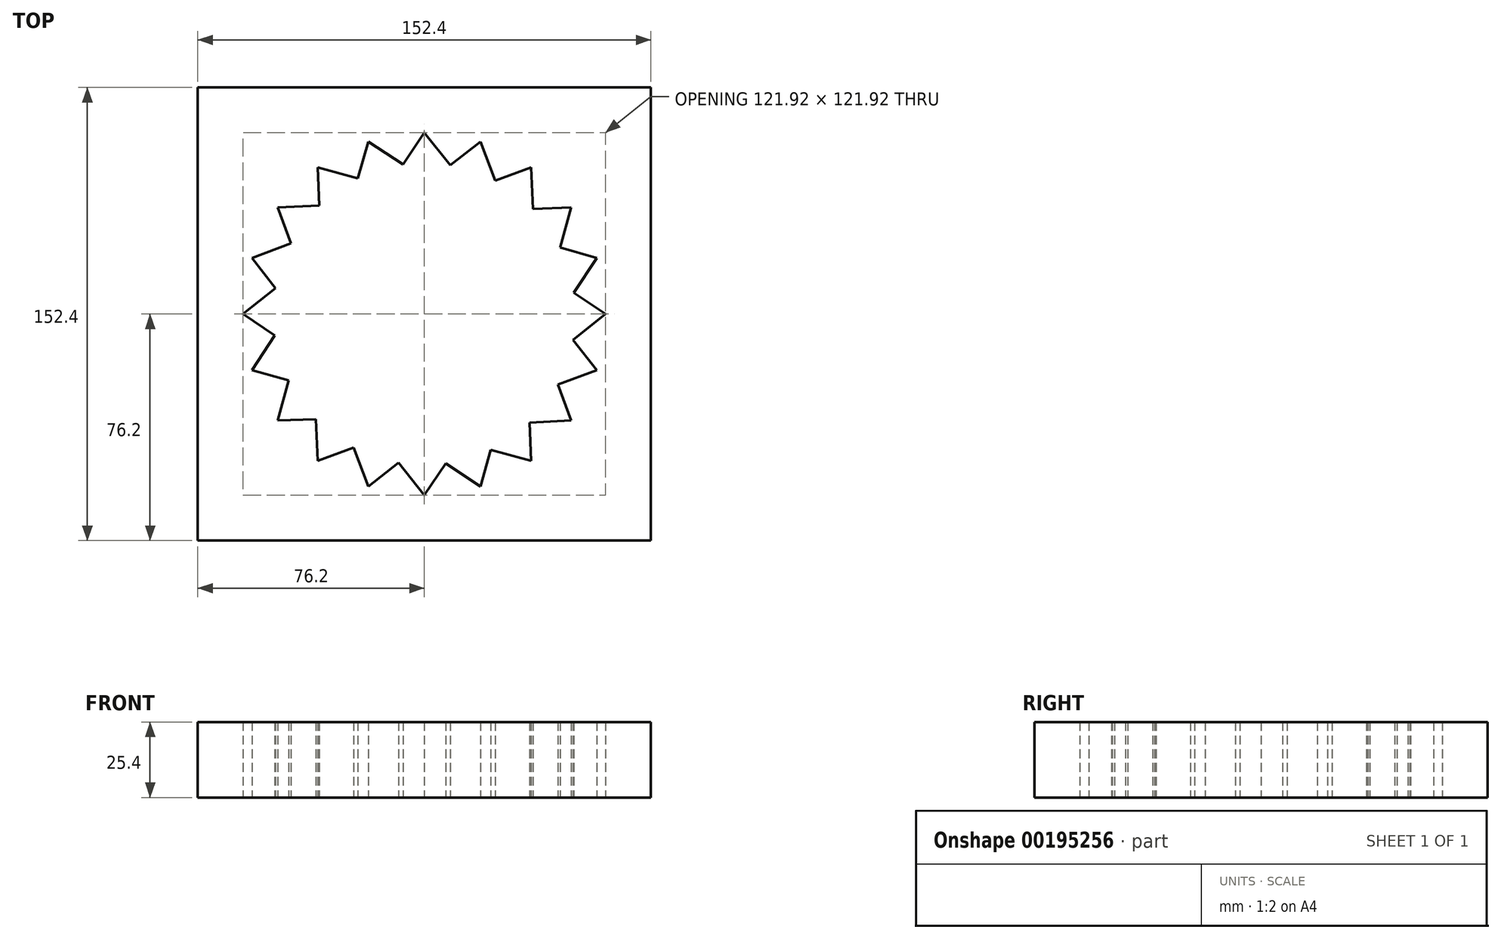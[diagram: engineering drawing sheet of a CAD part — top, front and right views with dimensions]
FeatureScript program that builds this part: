
annotation { "Feature Type Name" : "Feature", "Feature Type Description" : "" }
export const myFeature = defineFeature(function(context is Context, id is Id, definition is map)
    precondition{}
    {
        {
            var Q0;
            Q0=qCreatedBy(makeId("Top.planeOp"),FACE);
            var sketch = newSketch(context, id + "F0", { "sketchPlane" : qUnion([Q0])});
            skLineSegment(sketch, "E0.bottom", {"start": v(-76.2, -76.2) * mm, "end": v(76.2, -76.2) * mm});
            skLineSegment(sketch, "E0.top", {"start": v(-76.2, 76.2) * mm, "end": v(76.2, 76.2) * mm});
            skLineSegment(sketch, "E0.left", {"start": v(-76.2, -76.2) * mm, "end": v(-76.2, 76.2) * mm});
            skLineSegment(sketch, "E0.right", {"start": v(76.2, -76.2) * mm, "end": v(76.2, 76.2) * mm});
            skPoint(sketch, "E1", {"position": v(0, 50.8) * mm});
            skPoint(sketch, "E2", {"position": v(0, 60.96) * mm});
            skLineSegment(sketch, "E3", {"start": v(0, 60.96) * mm, "end": v(-7.15, 50.3) * mm});
            skLineSegment(sketch, "E4", {"start": v(8.74, 50.04) * mm, "end": v(0, 60.96) * mm});
            skLineSegment(sketch, "E5.1.0", {"start": v(-7.15, 50.3) * mm, "end": v(-18.84, 57.98) * mm});
            skLineSegment(sketch, "E5.1.1", {"start": v(-18.84, 57.98) * mm, "end": v(-22.35, 45.62) * mm});
            skLineSegment(sketch, "E5.2.0", {"start": v(-22.35, 45.62) * mm, "end": v(-35.83, 49.32) * mm});
            skLineSegment(sketch, "E5.2.1", {"start": v(-35.83, 49.32) * mm, "end": v(-35.35, 36.48) * mm});
            skLineSegment(sketch, "E5.3.0", {"start": v(-35.35, 36.48) * mm, "end": v(-49.32, 35.83) * mm});
            skLineSegment(sketch, "E5.3.1", {"start": v(-49.32, 35.83) * mm, "end": v(-44.9, 23.77) * mm});
            skLineSegment(sketch, "E5.4.0", {"start": v(-44.9, 23.77) * mm, "end": v(-57.98, 18.84) * mm});
            skLineSegment(sketch, "E5.4.1", {"start": v(-57.98, 18.84) * mm, "end": v(-50.04, 8.74) * mm});
            skLineSegment(sketch, "E5.5.0", {"start": v(-50.04, 8.74) * mm, "end": v(-60.96, 0) * mm});
            skLineSegment(sketch, "E5.5.1", {"start": v(-60.96, 0) * mm, "end": v(-50.3, -7.15) * mm});
            skLineSegment(sketch, "E5.6.0", {"start": v(-50.3, -7.15) * mm, "end": v(-57.98, -18.84) * mm});
            skLineSegment(sketch, "E5.6.1", {"start": v(-57.98, -18.84) * mm, "end": v(-45.62, -22.35) * mm});
            skLineSegment(sketch, "E5.7.0", {"start": v(-45.62, -22.35) * mm, "end": v(-49.32, -35.83) * mm});
            skLineSegment(sketch, "E5.7.1", {"start": v(-49.32, -35.83) * mm, "end": v(-36.48, -35.35) * mm});
            skLineSegment(sketch, "E5.8.0", {"start": v(-36.48, -35.35) * mm, "end": v(-35.83, -49.32) * mm});
            skLineSegment(sketch, "E5.8.1", {"start": v(-35.83, -49.32) * mm, "end": v(-23.77, -44.9) * mm});
            skLineSegment(sketch, "E5.9.0", {"start": v(-23.77, -44.9) * mm, "end": v(-18.84, -57.98) * mm});
            skLineSegment(sketch, "E5.9.1", {"start": v(-18.84, -57.98) * mm, "end": v(-8.74, -50.04) * mm});
            skLineSegment(sketch, "E5.10.0", {"start": v(-8.74, -50.04) * mm, "end": v(0, -60.96) * mm});
            skLineSegment(sketch, "E5.10.1", {"start": v(0, -60.96) * mm, "end": v(7.15, -50.3) * mm});
            skLineSegment(sketch, "E5.11.0", {"start": v(7.15, -50.3) * mm, "end": v(18.84, -57.98) * mm});
            skLineSegment(sketch, "E5.11.1", {"start": v(18.84, -57.98) * mm, "end": v(22.35, -45.62) * mm});
            skLineSegment(sketch, "E5.12.0", {"start": v(22.35, -45.62) * mm, "end": v(35.83, -49.32) * mm});
            skLineSegment(sketch, "E5.12.1", {"start": v(35.83, -49.32) * mm, "end": v(35.35, -36.48) * mm});
            skLineSegment(sketch, "E5.13.0", {"start": v(35.35, -36.48) * mm, "end": v(49.32, -35.83) * mm});
            skLineSegment(sketch, "E5.13.1", {"start": v(49.32, -35.83) * mm, "end": v(44.9, -23.77) * mm});
            skLineSegment(sketch, "E5.14.0", {"start": v(44.9, -23.77) * mm, "end": v(57.98, -18.84) * mm});
            skLineSegment(sketch, "E5.14.1", {"start": v(57.98, -18.84) * mm, "end": v(50.04, -8.74) * mm});
            skLineSegment(sketch, "E5.15.0", {"start": v(50.04, -8.74) * mm, "end": v(60.96, 0) * mm});
            skLineSegment(sketch, "E5.15.1", {"start": v(60.96, 0) * mm, "end": v(50.3, 7.15) * mm});
            skLineSegment(sketch, "E5.16.0", {"start": v(50.3, 7.15) * mm, "end": v(57.98, 18.84) * mm});
            skLineSegment(sketch, "E5.16.1", {"start": v(57.98, 18.84) * mm, "end": v(45.62, 22.35) * mm});
            skLineSegment(sketch, "E5.17.0", {"start": v(45.62, 22.35) * mm, "end": v(49.32, 35.83) * mm});
            skLineSegment(sketch, "E5.17.1", {"start": v(49.32, 35.83) * mm, "end": v(36.48, 35.35) * mm});
            skLineSegment(sketch, "E5.18.0", {"start": v(36.48, 35.35) * mm, "end": v(35.83, 49.32) * mm});
            skLineSegment(sketch, "E5.18.1", {"start": v(35.83, 49.32) * mm, "end": v(23.77, 44.9) * mm});
            skLineSegment(sketch, "E5.19.0", {"start": v(23.77, 44.9) * mm, "end": v(18.84, 57.98) * mm});
            skLineSegment(sketch, "E5.19.1", {"start": v(18.84, 57.98) * mm, "end": v(8.74, 50.04) * mm});
            skPoint(sketch, "E6", {"position": v(0, 35.56) * mm});
            skLineSegment(sketch, "E7.direction1", {"start": v(-7.15, 50.3) * mm, "end": v(18.25, 50.3) * mm, "construction": true});
            skLineSegment(sketch, "E8", {"start": v(0, 35.56) * mm, "end": v(-7.15, 24.64) * mm});
            skLineSegment(sketch, "E9", {"start": v(0, 35.56) * mm, "end": v(8.74, 24.64) * mm});
            skSolve(sketch);
        }
        {
            var Q0;
            Q0=makeQuery(id+"F0.imprint","IMPRINT",FACE,{"disambiguationData":[TD([[makeQuery(id+"F0.imprint","IMPRINT",EDGE,{"derivedFrom":sQuery(id+"F0.wireOp",EDGE,"E0.bottom")}),1.0]])]});
            extrude(context, id + "F1", {"entities" : qUnion([Q0]), "depth" : 25.4 * mm});
        }
    });
